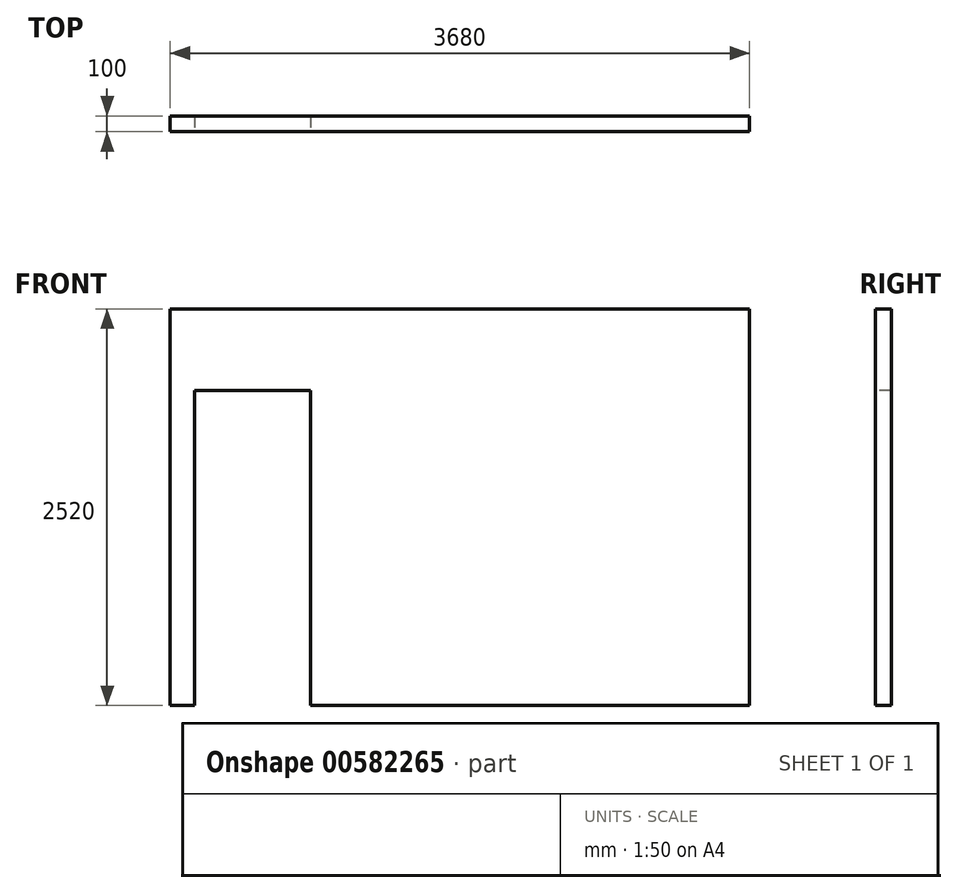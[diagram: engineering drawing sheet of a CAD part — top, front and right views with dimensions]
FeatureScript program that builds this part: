
annotation { "Feature Type Name" : "Feature", "Feature Type Description" : "" }
export const myFeature = defineFeature(function(context is Context, id is Id, definition is map)
    precondition{}
    {
        {
            var Q0;
            Q0=qCreatedBy(makeId("Front.planeOp"),FACE);
            var sketch = newSketch(context, id + "F0", { "sketchPlane" : qUnion([Q0])});
            skLineSegment(sketch, "E0.bottom", {"start": v(1840, 1260) * mm, "end": v(-1840, 1260) * mm});
            skLineSegment(sketch, "E0.top", {"start": v(1840, -1260) * mm, "end": v(-1840, -1260) * mm});
            skLineSegment(sketch, "E0.left", {"start": v(1840, 1260) * mm, "end": v(1840, -1260) * mm});
            skLineSegment(sketch, "E0.right", {"start": v(-1840, 1260) * mm, "end": v(-1840, -1260) * mm});
            skPoint(sketch, "E0.middle", {"position": v(0, 0) * mm});
            skSolve(sketch);
        }
        {
            var Q0;
            Q0=makeQuery(id+"F0.imprint","IMPRINT",FACE,{"disambiguationData":[TD([[makeQuery(id+"F0.imprint","IMPRINT",EDGE,{"derivedFrom":sQuery(id+"F0.wireOp",EDGE,"E0.bottom")}),1.0]])]});
            extrude(context, id + "F1", {"entities" : qUnion([Q0]), "oppositeDirection" : true, "depth" : 100 * mm, "offsetDistance" : 25 * mm});
        }
        {
            var Q0;
            Q0=makeQuery(id+"F1.opExtrude","CAP_FACE",FACE,{"disambiguationData":[OSD([sQuery(id+"F0.wireOp",EDGE,"E0.bottom"),sQuery(id+"F0.wireOp",EDGE,"E0.top"),sQuery(id+"F0.wireOp",EDGE,"E0.left"),sQuery(id+"F0.wireOp",EDGE,"E0.right")])],"isStart":true});
            var sketch = newSketch(context, id + "F2", { "sketchPlane" : qUnion([Q0])});
            skLineSegment(sketch, "E1.bottom", {"start": v(-1685, -1260) * mm, "end": v(-950, -1260) * mm});
            skLineSegment(sketch, "E1.top", {"start": v(-1685, 740) * mm, "end": v(-950, 740) * mm});
            skLineSegment(sketch, "E1.left", {"start": v(-1685, -1260) * mm, "end": v(-1685, 740) * mm});
            skLineSegment(sketch, "E1.right", {"start": v(-950, -1260) * mm, "end": v(-950, 740) * mm});
            skSolve(sketch);
        }
        {
            var Q0;
            Q0=makeQuery(id+"F2.imprint","IMPRINT",FACE,{"disambiguationData":[TD([[makeQuery(id+"F2.imprint","IMPRINT",EDGE,{"derivedFrom":sQuery(id+"F2.wireOp",EDGE,"E1.bottom")}),-1.0]])]});
            extrude(context, id + "F3", {"entities" : qUnion([Q0]), "operationType" : NewBodyOperationType.REMOVE, "oppositeDirection" : true, "depth" : 100 * mm, "offsetDistance" : 25 * mm});
        }
    });
